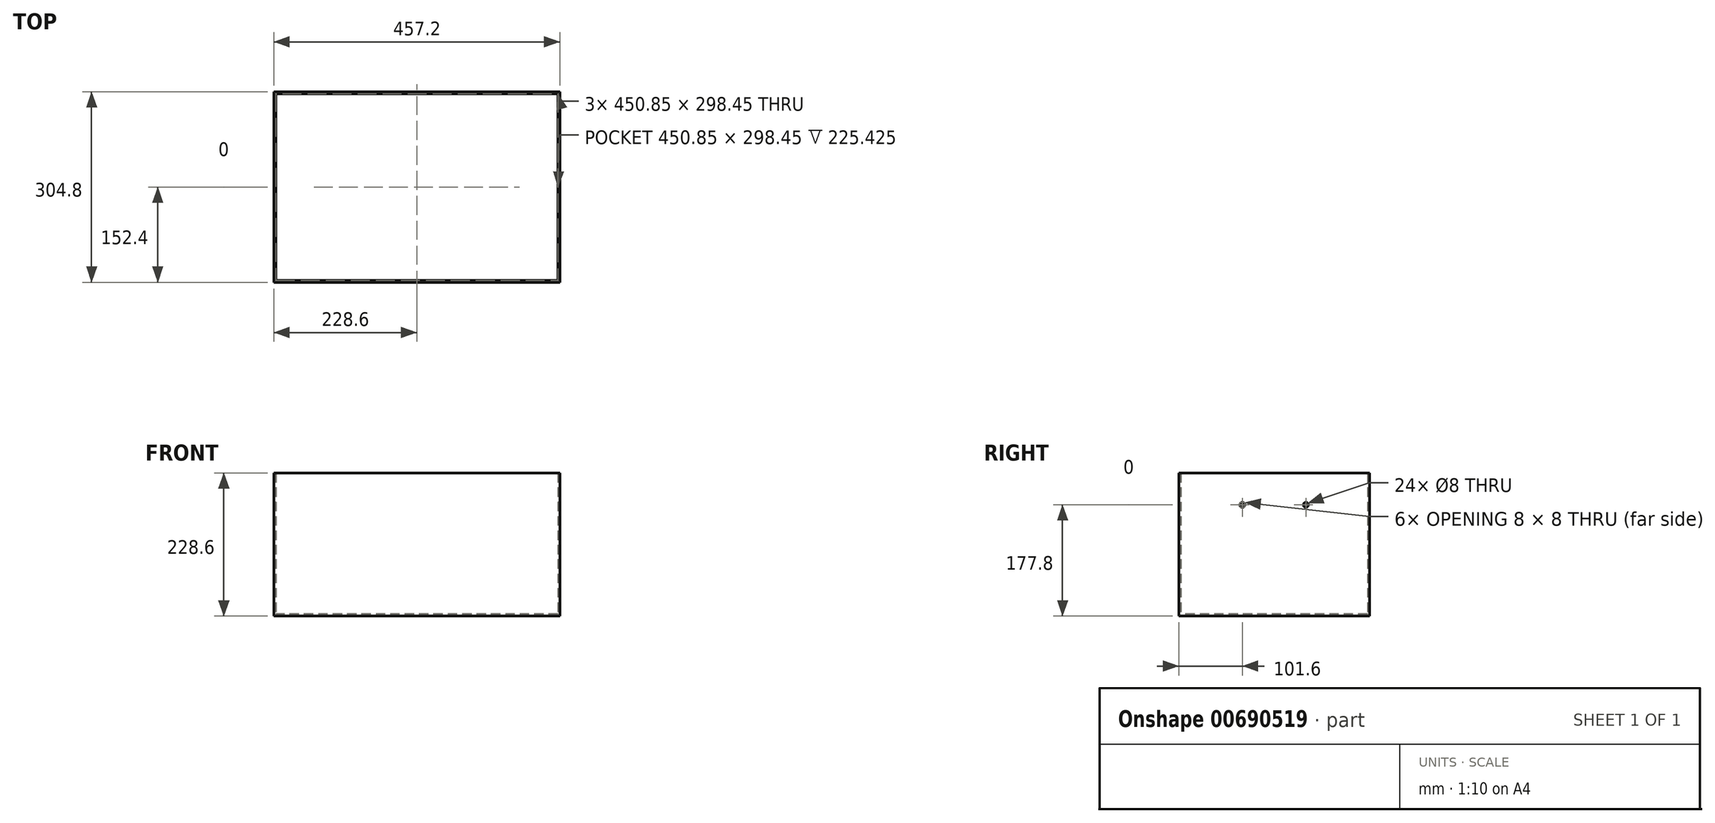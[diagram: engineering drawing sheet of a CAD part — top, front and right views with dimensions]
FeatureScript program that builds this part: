
annotation { "Feature Type Name" : "Feature", "Feature Type Description" : "" }
export const myFeature = defineFeature(function(context is Context, id is Id, definition is map)
    precondition{}
    {
        {
            var Q0;
            Q0=qCreatedBy(makeId("Top.planeOp"),FACE);
            var sketch = newSketch(context, id + "F0", { "sketchPlane" : qUnion([Q0])});
            skLineSegment(sketch, "E0", {"start": v(0, 0) * mm, "end": v(0, -304.8) * mm});
            skLineSegment(sketch, "E1", {"start": v(0, -304.8) * mm, "end": v(457.2, -304.8) * mm});
            skLineSegment(sketch, "E2", {"start": v(457.2, -304.8) * mm, "end": v(457.2, 0) * mm});
            skLineSegment(sketch, "E3", {"start": v(457.2, 0) * mm, "end": v(0, 0) * mm});
            skSolve(sketch);
        }
        {
            var Q0;
            Q0 = qSketchRegion(id + "F0", true);
            extrude(context, id + "F1", {"entities" : qUnion([Q0]), "depth" : 228.6 * mm, "offsetDistance" : 25.4 * mm});
        }
        {
            var Q0;
            Q0=makeQuery(id+"F1.opExtrude","CAP_FACE",FACE,{"disambiguationData":[OSD([sQuery(id+"F0.wireOp",EDGE,"E0"),sQuery(id+"F0.wireOp",EDGE,"E1"),sQuery(id+"F0.wireOp",EDGE,"E2"),sQuery(id+"F0.wireOp",EDGE,"E3")])],"isStart":false});
            shell(context, id + "F2", {"entities" : qUnion([Q0]), "thickness" : 3.17 * mm});
        }
        {
            var Q0;
            Q0=makeQuery(id+"F1.opExtrude","SWEPT_FACE",FACE,{"disambiguationData":[OSD([sQuery(id+"F0.wireOp",EDGE,"E0")])]});
            var sketch = newSketch(context, id + "F3", { "sketchPlane" : qUnion([Q0])});
            skLineSegment(sketch, "E4", {"start": v(0, 0) * mm, "end": v(0, 12.61) * mm});
            skLineSegment(sketch, "E5", {"start": v(0, 177.8) * mm, "end": v(101.6, 177.8) * mm});
            skLineSegment(sketch, "E6", {"start": v(101.6, 177.8) * mm, "end": v(203.2, 177.8) * mm});
            skSolve(sketch);
        }
        {
            var Q0;
            Q0=sQuery(id+"F3.wireOp",VERTEX,"E6.end");
            var Q1;
            Q1=sQuery(id+"F3.wireOp",VERTEX,"E6.start");
            var Q2;
            Q2=makeQuery(id+"F1.opExtrude","SWEPT_BODY",BODY,{"disambiguationData":[OSD([sQuery(id+"F0.wireOp",EDGE,"E0"),sQuery(id+"F0.wireOp",EDGE,"E1"),sQuery(id+"F0.wireOp",EDGE,"E2"),sQuery(id+"F0.wireOp",EDGE,"E3")])]});
            hole(context, id + "F4", {"style" : HoleStyle.SIMPLE, "endStyle" : HoleEndStyle.THROUGH, "holeDiameter" : 8 * mm, "majorDiameter" : 6.35 * mm, "isTappedThrough" : true, "tappedDepth" : 12.7 * mm, "tapClearance" : 3, "locations" : qUnion([Q0, Q1]), "scope" : qUnion([Q2])});
        }
    });
